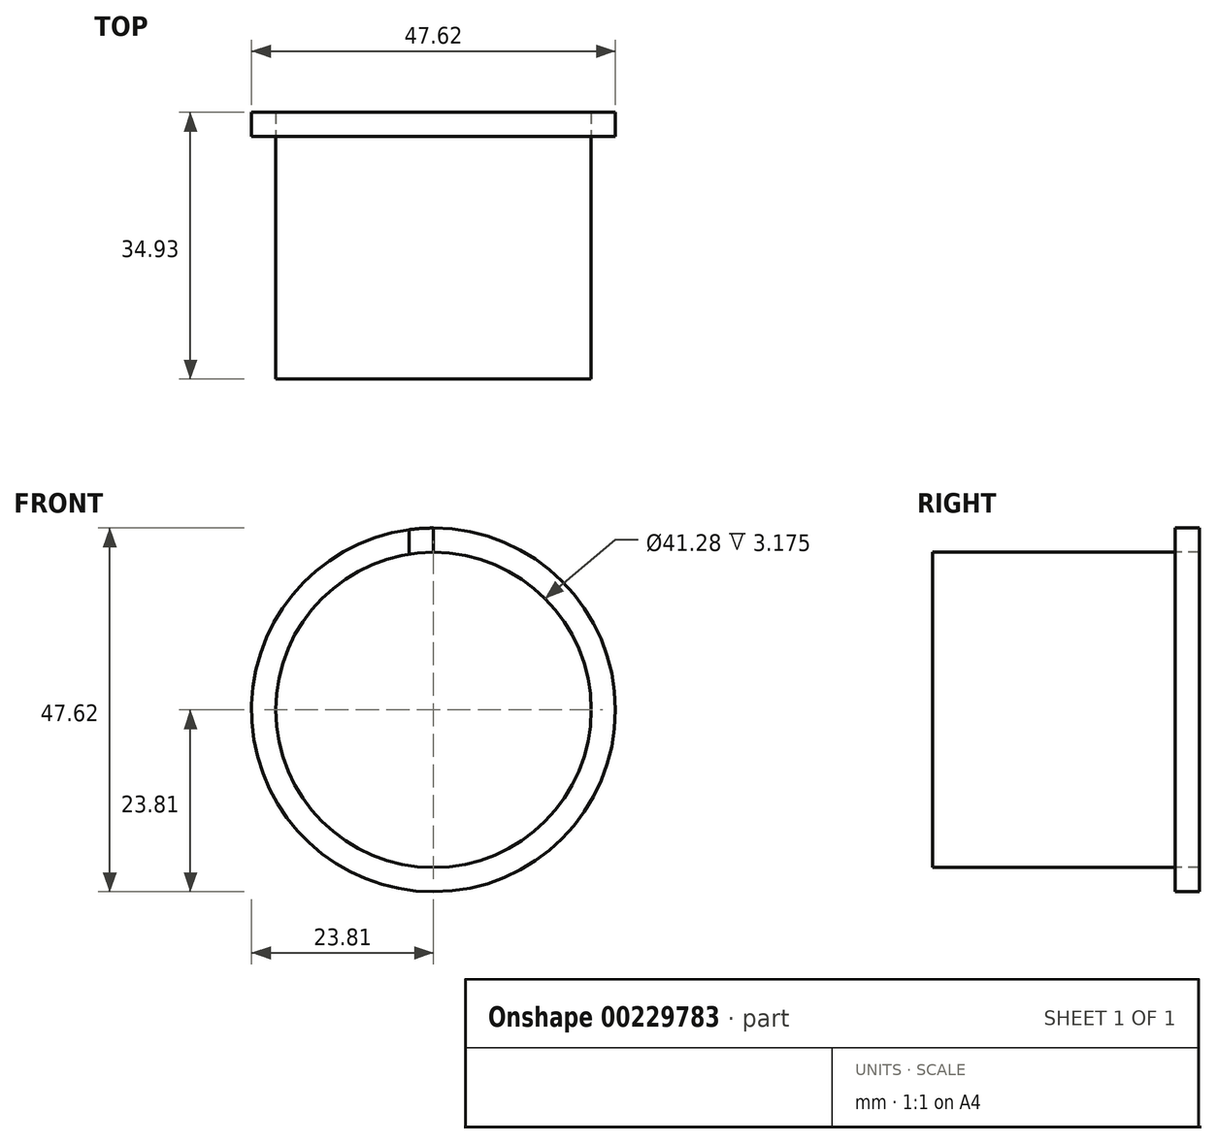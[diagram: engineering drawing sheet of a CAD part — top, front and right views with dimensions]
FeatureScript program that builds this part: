
annotation { "Feature Type Name" : "Feature", "Feature Type Description" : "" }
export const myFeature = defineFeature(function(context is Context, id is Id, definition is map)
    precondition{}
    {
        {
            assignVariable(context, id + "F0", {"name" : "depth", "anyValue" : 31.75 * mm});
        }
        {
            assignVariable(context, id + "F1", {"name" : "ribLength", "anyValue" : 1 / 203.2 * mm});
        }
        {
            var Q0;
            Q0=qCreatedBy(makeId("Front.planeOp"),FACE);
            var sketch = newSketch(context, id + "F2", { "sketchPlane" : qUnion([Q0])});
            skCircle(sketch, "E0", {"center": v(0, 0) * mm, "radius": 20.64 * mm});
            skCircle(sketch, "E1", {"center": v(0, 0) * mm, "radius": 23.81 * mm});
            skLineSegment(sketch, "E2", {"start": v(-3.18, 23.6) * mm, "end": v(-3.18, 20.4) * mm});
            skLineSegment(sketch, "E3", {"start": v(0, 23.81) * mm, "end": v(0, 20.4) * mm});
            skSolve(sketch);
        }
        {
            var Q0;
            Q0 = qSketchRegion(id + "F2", true);
            extrude(context, id + "F3", {"entities" : qUnion([Q0]), "oppositeDirection" : true, "depth" : 3.17 * mm});
        }
        {
            var Q0;
            {var subQ0=sQuery(id+"F2.wireOp",EDGE,"E0");var subQ1=makeQuery(id+"F2.imprint","INTERSECT",VERTEX,{"derivedFrom":[subQ0,sQuery(id+"F2.wireOp",EDGE,"E2")]});Q0=makeQuery(id+"F2.imprint","IMPRINT",FACE,{"disambiguationData":[TD([[makeQuery(id+"F2.imprint","IMPRINT",EDGE,{"disambiguationData":[TD([[subQ1,1.0]])],"derivedFrom":subQ0}),1.0]])]});}
            extrude(context, id + "F4", {"entities" : qUnion([Q0]), "depth" : getVariable(context, 'depth')});
        }
        {
            var Q0;
            {var subQ0=sQuery(id+"F2.wireOp",EDGE,"E2");Q0=makeQuery(id+"F2.imprint","IMPRINT",FACE,{"disambiguationData":[TD([[makeQuery(id+"F2.imprint","IMPRINT",EDGE,{"derivedFrom":subQ0}),1.0]])]});}
            extrude(context, id + "F5", {"entities" : qUnion([Q0]), "depth" : getVariable(context, 'ribLength')});
        }
        {
            var Q0;
            {var subQ0=sQuery(id+"F2.wireOp",EDGE,"E0");var subQ1=makeQuery(id+"F2.imprint","INTERSECT",VERTEX,{"derivedFrom":[subQ0,sQuery(id+"F2.wireOp",EDGE,"E2")]});Q0=makeQuery(id+"F2.imprint","IMPRINT",FACE,{"disambiguationData":[TD([[makeQuery(id+"F2.imprint","IMPRINT",EDGE,{"disambiguationData":[TD([[subQ1,1.0]])],"derivedFrom":subQ0}),1.0]])]});}
            extrude(context, id + "F6", {"entities" : qUnion([Q0]), "oppositeDirection" : true, "depth" : 3.17 * mm});
        }
    });
